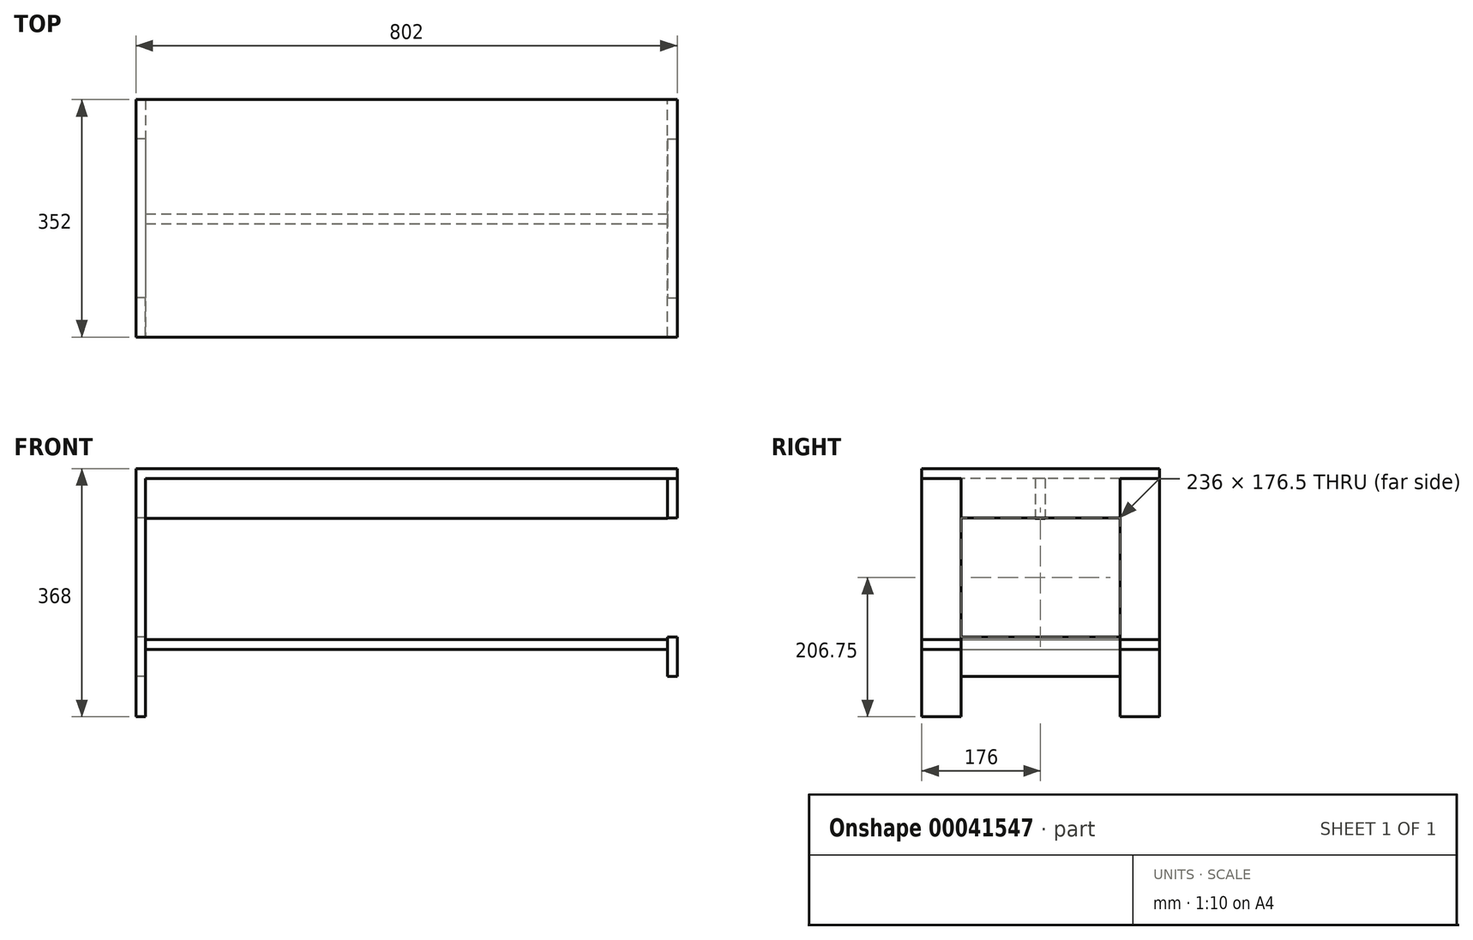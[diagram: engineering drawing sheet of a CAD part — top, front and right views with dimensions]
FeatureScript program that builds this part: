
annotation { "Feature Type Name" : "Feature", "Feature Type Description" : "" }
export const myFeature = defineFeature(function(context is Context, id is Id, definition is map)
    precondition{}
    {
        {
            assignVariable(context, id + "F0", {"name" : "t", "anyValue" : 14.5});
        }
        {
            var Q0;
            Q0=qCreatedBy(makeId("Top.planeOp"),FACE);
            cPlane(context, id + "F1", {"entities" : qUnion([Q0]), "cplaneType" : CPlaneType.OFFSET, "offset" : 368 * mm, "width" : 150 * mm, "height" : 150 * mm});
        }
        {
            var Q0;
            Q0=qCreatedBy(id+"F1.planeOp",FACE);
            var sketch = newSketch(context, id + "F2", { "sketchPlane" : qUnion([Q0])});
            skLineSegment(sketch, "E0.bottom", {"start": v(-401, 0) * mm, "end": v(401, 0) * mm});
            skLineSegment(sketch, "E0.top", {"start": v(-401, -352) * mm, "end": v(401, -352) * mm});
            skLineSegment(sketch, "E0.left", {"start": v(-401, 0) * mm, "end": v(-401, -352) * mm});
            skLineSegment(sketch, "E0.right", {"start": v(401, 0) * mm, "end": v(401, -352) * mm});
            skSolve(sketch);
        }
        {
            var Q0;
            Q0=sQuery(id+"F2.wireOp",EDGE,"E0.left");
            cPlane(context, id + "F3", {"entities" : qUnion([Q0]), "cplaneType" : CPlaneType.MID_PLANE, "offset" : 150 * mm, "width" : 150 * mm, "height" : 150 * mm});
        }
        {
            var Q0;
            Q0=sQuery(id+"F2.wireOp",EDGE,"E0.left");
            var Q1;
            Q1=qCreatedBy(makeId("Right.planeOp"),FACE);
            cPlane(context, id + "F4", {"entities" : qUnion([Q0, Q1]), "cplaneType" : CPlaneType.LINE_ANGLE, "offset" : 150 * mm, "angle" : 0 * degree, "width" : 150 * mm, "height" : 150 * mm});
        }
        {
            var Q0;
            Q0=makeQuery(id+"F2.imprint","IMPRINT",FACE,{"disambiguationData":[TD([[makeQuery(id+"F2.imprint","IMPRINT",EDGE,{"derivedFrom":sQuery(id+"F2.wireOp",EDGE,"E0.bottom")}),-1.0]])]});
            extrude(context, id + "F5", {"entities" : qUnion([Q0]), "oppositeDirection" : true, "depth" : (getVariable(context, 't')) * mm});
        }
        {
            var Q0;
            Q0=qCreatedBy(id+"F4.planeOp",FACE);
            var sketch = newSketch(context, id + "F6", { "sketchPlane" : qUnion([Q0])});
            skLineSegment(sketch, "E1.bottom", {"start": v(0, 0) * mm, "end": v(58, 0) * mm});
            skLineSegment(sketch, "E1.top", {"start": v(0, 353.5) * mm, "end": v(58, 353.5) * mm});
            skLineSegment(sketch, "E1.left", {"start": v(0, 0) * mm, "end": v(0, 353.5) * mm});
            skLineSegment(sketch, "E1.right", {"start": v(58, 0) * mm, "end": v(58, 353.5) * mm});
            skSolve(sketch);
        }
        {
            var Q0;
            Q0=makeQuery(id+"F6.imprint","IMPRINT",FACE,{"disambiguationData":[TD([[makeQuery(id+"F6.imprint","IMPRINT",EDGE,{"derivedFrom":sQuery(id+"F6.wireOp",EDGE,"E1.bottom")}),1.0]])]});
            extrude(context, id + "F7", {"entities" : qUnion([Q0]), "oppositeDirection" : true, "depth" : (getVariable(context, 't')) * mm});
        }
        {
            var Q0;
            Q0=makeQuery(id+"F7.opExtrude","SWEPT_BODY",BODY,{"disambiguationData":[OSD([sQuery(id+"F6.wireOp",EDGE,"E1.bottom"),sQuery(id+"F6.wireOp",EDGE,"E1.top"),sQuery(id+"F6.wireOp",EDGE,"E1.left"),sQuery(id+"F6.wireOp",EDGE,"E1.right")])]});
            var Q1;
            Q1=qCreatedBy(id+"F3.planeOp",FACE);
            mirror(context, id + "F8", {"operationType" : NewBodyOperationType.ADD, "entities" : qUnion([Q0]), "mirrorPlane" : qUnion([Q1])});
        }
        {
            var Q0;
            Q0=qCreatedBy(id+"F4.planeOp",FACE);
            var sketch = newSketch(context, id + "F9", { "sketchPlane" : qUnion([Q0])});
            skLineSegment(sketch, "E2.bottom", {"start": v(58, 353.5) * mm, "end": v(294, 353.5) * mm});
            skLineSegment(sketch, "E2.top", {"start": v(58, 295) * mm, "end": v(294, 295) * mm});
            skLineSegment(sketch, "E2.left", {"start": v(58, 353.5) * mm, "end": v(58, 295) * mm});
            skLineSegment(sketch, "E2.right", {"start": v(294, 353.5) * mm, "end": v(294, 295) * mm});
            skPoint(sketch, "E3", {"position": v(176, 353.5) * mm});
            skSolve(sketch);
        }
        {
            var Q0;
            Q0=makeQuery(id+"F9.imprint","IMPRINT",FACE,{"disambiguationData":[TD([[makeQuery(id+"F9.imprint","IMPRINT",EDGE,{"derivedFrom":sQuery(id+"F9.wireOp",EDGE,"E2.bottom")}),-1.0]])]});
            extrude(context, id + "F10", {"entities" : qUnion([Q0]), "oppositeDirection" : true, "depth" : (getVariable(context, 't')) * mm});
        }
        {
            var Q0;
            Q0=makeQuery(id+"F10.opExtrude","SWEPT_BODY",BODY,{"disambiguationData":[OSD([sQuery(id+"F9.wireOp",EDGE,"E2.bottom"),sQuery(id+"F9.wireOp",EDGE,"E2.top"),sQuery(id+"F9.wireOp",EDGE,"E2.left"),sQuery(id+"F9.wireOp",EDGE,"E2.right")])]});
            transform(context, id + "F11", {"entities" : qUnion([Q0]), "transformType" : TransformType.TRANSLATION_3D, "dx" : 0 * mm, "dy" : 0 * mm, "dz" : (60 - 295) * mm, "makeCopy" : true});
        }
        {
            var Q0;
            Q0=makeQuery(id+"F7.opExtrude","SWEPT_BODY",BODY,{"disambiguationData":[OSD([sQuery(id+"F6.wireOp",EDGE,"E1.bottom"),sQuery(id+"F6.wireOp",EDGE,"E1.top"),sQuery(id+"F6.wireOp",EDGE,"E1.left"),sQuery(id+"F6.wireOp",EDGE,"E1.right")])]});
            var Q1;
            Q1=makeQuery(id+"F8.opPattern","COPY",BODY,{"derivedFrom":makeQuery(id+"F7.opExtrude","SWEPT_BODY",BODY,{"disambiguationData":[OSD([sQuery(id+"F6.wireOp",EDGE,"E1.bottom"),sQuery(id+"F6.wireOp",EDGE,"E1.top"),sQuery(id+"F6.wireOp",EDGE,"E1.left"),sQuery(id+"F6.wireOp",EDGE,"E1.right")])]}),"instanceName":"1"});
            var Q2;
            Q2=makeQuery(id+"F10.opExtrude","SWEPT_BODY",BODY,{"disambiguationData":[OSD([sQuery(id+"F9.wireOp",EDGE,"E2.bottom"),sQuery(id+"F9.wireOp",EDGE,"E2.top"),sQuery(id+"F9.wireOp",EDGE,"E2.left"),sQuery(id+"F9.wireOp",EDGE,"E2.right")])]});
            var Q3;
            Q3=makeQuery(id+"F11.opPattern","COPY",BODY,{"derivedFrom":makeQuery(id+"F10.opExtrude","SWEPT_BODY",BODY,{"disambiguationData":[OSD([sQuery(id+"F9.wireOp",EDGE,"E2.bottom"),sQuery(id+"F9.wireOp",EDGE,"E2.top"),sQuery(id+"F9.wireOp",EDGE,"E2.left"),sQuery(id+"F9.wireOp",EDGE,"E2.right")])]}),"instanceName":"1"});
            var Q4;
            Q4=qCreatedBy(makeId("Right.planeOp"),FACE);
            mirror(context, id + "F12", {"operationType" : NewBodyOperationType.ADD, "entities" : qUnion([Q0, Q1, Q2, Q3]), "mirrorPlane" : qUnion([Q4])});
        }
        {
            var Q0;
            Q0=qCreatedBy(makeId("Front.planeOp"),FACE);
            var sketch = newSketch(context, id + "F13", { "sketchPlane" : qUnion([Q0])});
            skLineSegment(sketch, "E4.bottom", {"start": v(-386.5, 114.5) * mm, "end": v(386.5, 114.5) * mm});
            skLineSegment(sketch, "E4.top", {"start": v(-386.5, 100) * mm, "end": v(386.5, 100) * mm});
            skLineSegment(sketch, "E4.left", {"start": v(-386.5, 114.5) * mm, "end": v(-386.5, 100) * mm});
            skLineSegment(sketch, "E4.right", {"start": v(386.5, 114.5) * mm, "end": v(386.5, 100) * mm});
            skPoint(sketch, "E5", {"position": v(0, 114.5) * mm});
            skSolve(sketch);
        }
        {
            var Q0;
            Q0=makeQuery(id+"F5.opExtrude","SWEPT_FACE",FACE,{"disambiguationData":[OSD([sQuery(id+"F2.wireOp",EDGE,"E0.top")])]});
            cPlane(context, id + "F14", {"entities" : qUnion([Q0]), "cplaneType" : CPlaneType.OFFSET, "offset" : 168 * mm, "oppositeDirection" : true, "width" : 150 * mm, "height" : 150 * mm});
        }
        {
            var Q0;
            Q0=qCreatedBy(id+"F14.planeOp",FACE);
            var sketch = newSketch(context, id + "F15", { "sketchPlane" : qUnion([Q0])});
            skLineSegment(sketch, "E6.bottom", {"start": v(-386.5, 353.5) * mm, "end": v(386.5, 353.5) * mm});
            skLineSegment(sketch, "E6.top", {"start": v(-386.5, 294.5) * mm, "end": v(386.5, 294.5) * mm});
            skLineSegment(sketch, "E6.left", {"start": v(-386.5, 353.5) * mm, "end": v(-386.5, 294.5) * mm});
            skLineSegment(sketch, "E6.right", {"start": v(386.5, 353.5) * mm, "end": v(386.5, 294.5) * mm});
            skSolve(sketch);
        }
        {
            var Q0;
            Q0=makeQuery(id+"F15.imprint","IMPRINT",FACE,{"disambiguationData":[TD([[makeQuery(id+"F15.imprint","IMPRINT",EDGE,{"derivedFrom":sQuery(id+"F15.wireOp",EDGE,"E6.bottom")}),-1.0]])]});
            extrude(context, id + "F16", {"entities" : qUnion([Q0]), "oppositeDirection" : true, "depth" : (getVariable(context, 't')) * mm});
        }
        {
            var Q0;
            Q0=makeQuery(id+"F13.imprint","IMPRINT",FACE,{"disambiguationData":[TD([[makeQuery(id+"F13.imprint","IMPRINT",EDGE,{"derivedFrom":sQuery(id+"F13.wireOp",EDGE,"E4.bottom")}),-1.0]])]});
            var Q1;
            Q1=makeQuery(id+"F5.opExtrude","SWEPT_FACE",FACE,{"disambiguationData":[OSD([sQuery(id+"F2.wireOp",EDGE,"E0.top")])]});
            extrude(context, id + "F17", {"entities" : qUnion([Q0]), "endBound" : BoundingType.UP_TO_SURFACE, "endBoundEntityFace" : qUnion([Q1]), "depth" : 25 * mm});
        }
    });
